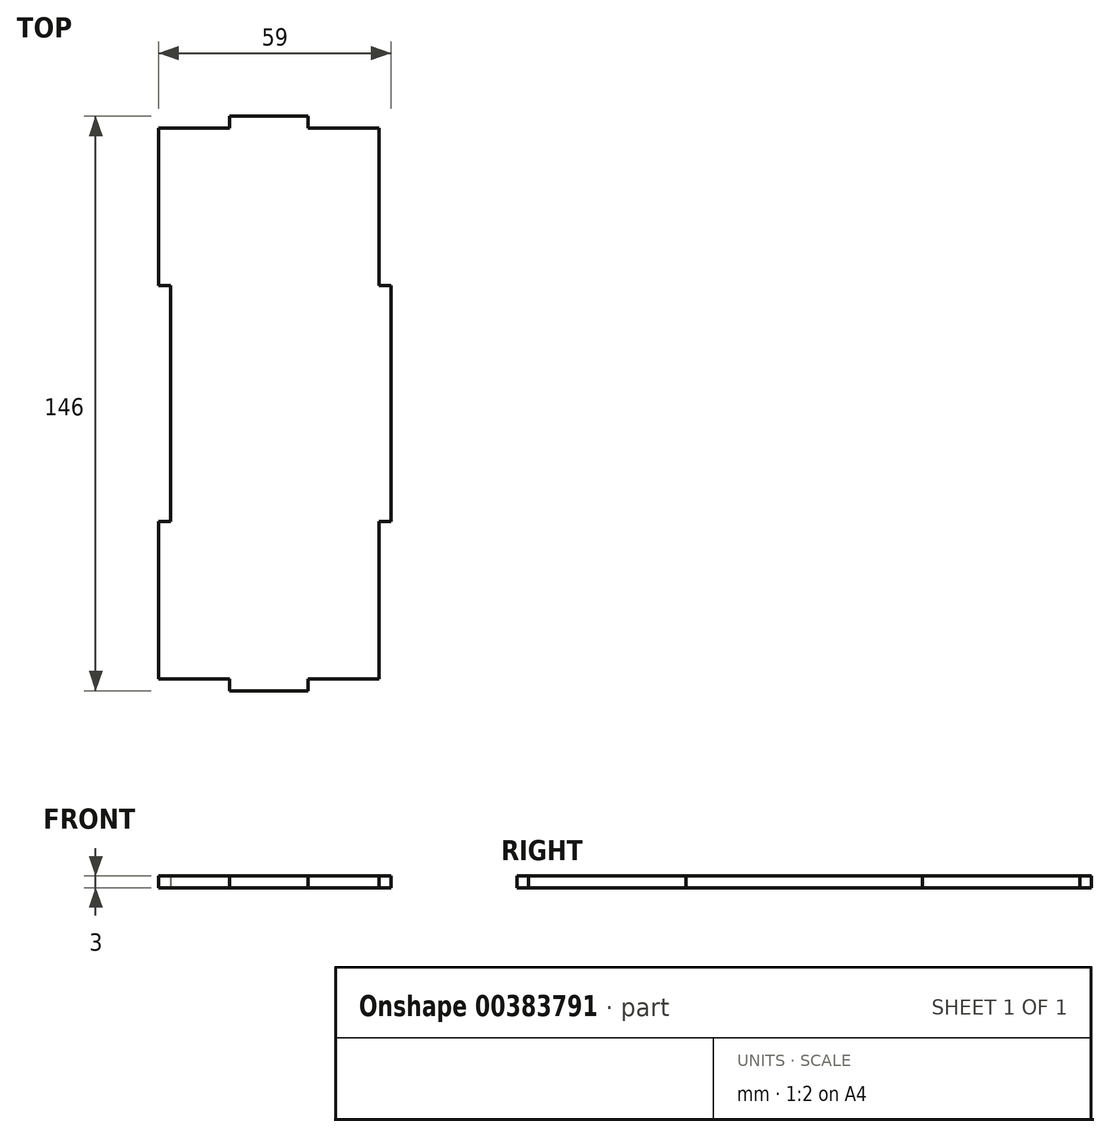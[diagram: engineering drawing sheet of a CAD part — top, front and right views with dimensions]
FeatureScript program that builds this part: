
annotation { "Feature Type Name" : "Feature", "Feature Type Description" : "" }
export const myFeature = defineFeature(function(context is Context, id is Id, definition is map)
    precondition{}
    {
        {
            var Q0;
            Q0=qCreatedBy(makeId("Top.planeOp"),FACE);
            var sketch = newSketch(context, id + "F0", { "sketchPlane" : qUnion([Q0])});
            skLineSegment(sketch, "E0.bottom", {"start": v(28, -70) * mm, "end": v(10, -70) * mm});
            skLineSegment(sketch, "E0.top", {"start": v(28, 70) * mm, "end": v(10, 70) * mm});
            skLineSegment(sketch, "E0.left", {"start": v(28, -70) * mm, "end": v(28, -30) * mm});
            skLineSegment(sketch, "E0.right", {"start": v(-28, -70) * mm, "end": v(-28, -30) * mm});
            skPoint(sketch, "E0.middle", {"position": v(0, 0) * mm});
            skLineSegment(sketch, "E1.bottom", {"start": v(-25, -30) * mm, "end": v(-28, -30) * mm});
            skLineSegment(sketch, "E1.top", {"start": v(-25, 30) * mm, "end": v(-31, 30) * mm});
            skLineSegment(sketch, "E1.left", {"start": v(-25, -30) * mm, "end": v(-25, 30) * mm});
            skPoint(sketch, "E1.middle", {"position": v(-28, 0) * mm});
            skLineSegment(sketch, "E2.trimOffspring", {"start": v(-28, 30) * mm, "end": v(-28, 70) * mm});
            skPoint(sketch, "E1.right.start.orphan", {"position": v(-31, -30) * mm});
            skLineSegment(sketch, "E3.bottom", {"start": v(31, -30) * mm, "end": v(28, -30) * mm});
            skLineSegment(sketch, "E3.top", {"start": v(31, 30) * mm, "end": v(28, 30) * mm});
            skLineSegment(sketch, "E3.left", {"start": v(31, -30) * mm, "end": v(31, 30) * mm});
            skPoint(sketch, "E3.middle", {"position": v(28, 0) * mm});
            skPoint(sketch, "E4.orphan", {"position": v(25, -30) * mm});
            skLineSegment(sketch, "E5.trimOffspring", {"start": v(28, 30) * mm, "end": v(28, 70) * mm});
            skPoint(sketch, "E6.orphan", {"position": v(25, 30) * mm});
            skLineSegment(sketch, "E7.bottom", {"start": v(10, 73) * mm, "end": v(-10, 73) * mm});
            skLineSegment(sketch, "E7.left", {"start": v(10, 73) * mm, "end": v(10, 70) * mm});
            skLineSegment(sketch, "E7.right", {"start": v(-10, 73) * mm, "end": v(-10, 70) * mm});
            skPoint(sketch, "E7.middle", {"position": v(0, 70) * mm});
            skLineSegment(sketch, "E8.trimOffspring", {"start": v(-10, 70) * mm, "end": v(-28, 70) * mm});
            skPoint(sketch, "E7.top.end.orphan", {"position": v(-10, 67) * mm});
            skPoint(sketch, "E7.top.start.orphan", {"position": v(10, 67) * mm});
            skLineSegment(sketch, "E9.top", {"start": v(10, -73) * mm, "end": v(-10, -73) * mm});
            skLineSegment(sketch, "E9.left", {"start": v(10, -70) * mm, "end": v(10, -73) * mm});
            skLineSegment(sketch, "E9.right", {"start": v(-10, -70) * mm, "end": v(-10, -73) * mm});
            skPoint(sketch, "E9.middle", {"position": v(0, -70) * mm});
            skPoint(sketch, "E10.orphan", {"position": v(-10, -67) * mm});
            skLineSegment(sketch, "E11.trimOffspring", {"start": v(-10, -70) * mm, "end": v(-28, -70) * mm});
            skPoint(sketch, "E12.orphan", {"position": v(10, -67) * mm});
            skSolve(sketch);
        }
        {
            var Q0;
            Q0 = qSketchRegion(id + "F0", true);
            extrude(context, id + "F1", {"entities" : qUnion([Q0]), "depth" : 3 * mm});
        }
    });
